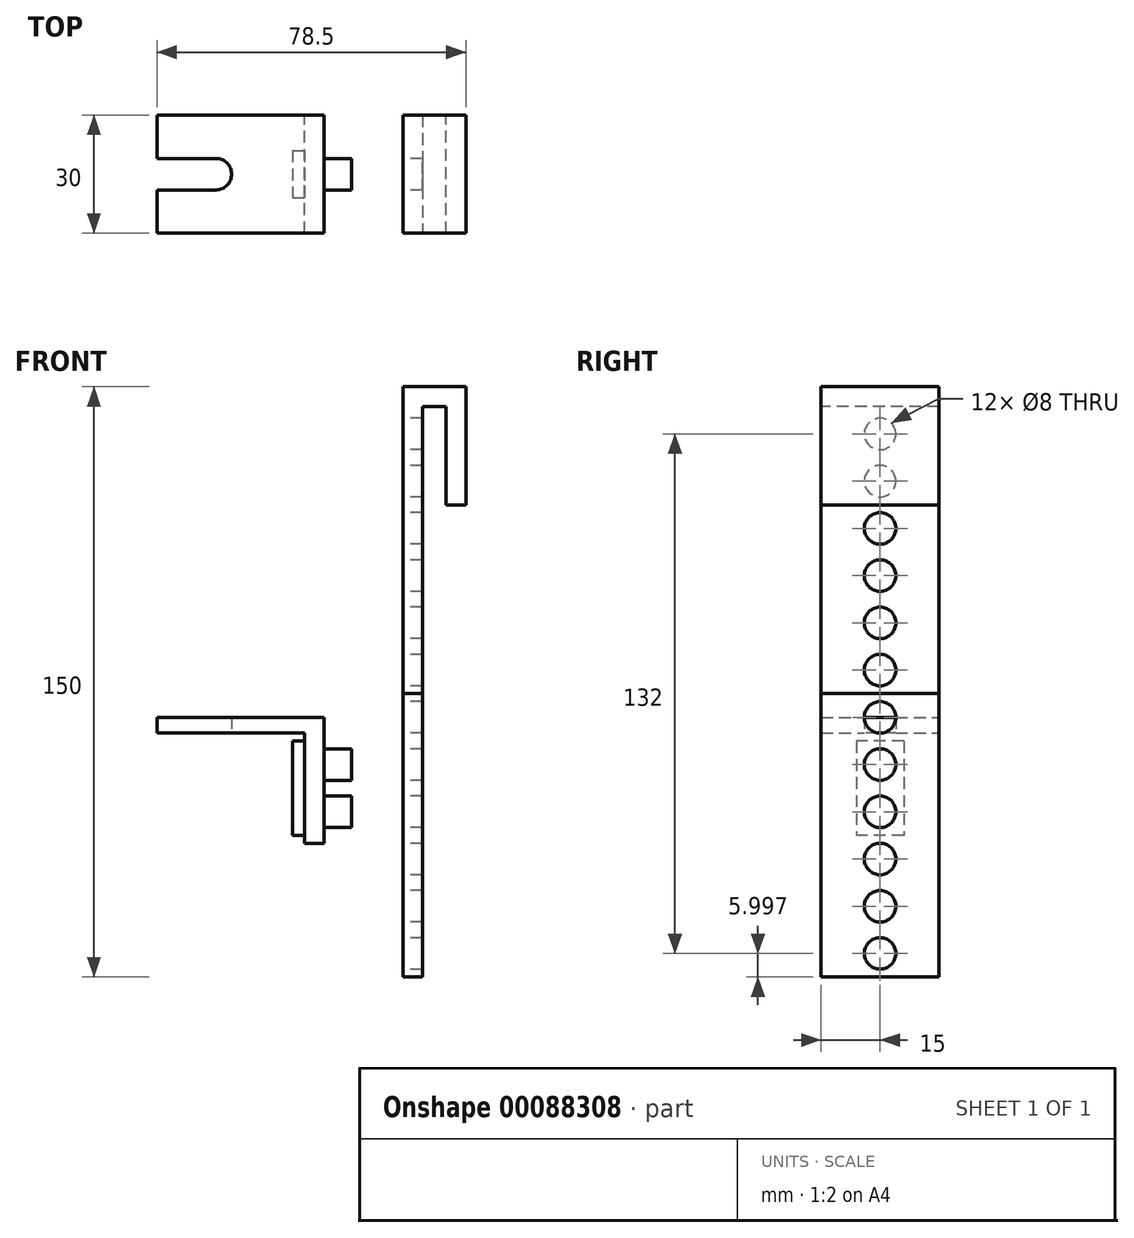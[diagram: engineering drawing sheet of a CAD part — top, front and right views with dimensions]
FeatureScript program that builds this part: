
annotation { "Feature Type Name" : "Feature", "Feature Type Description" : "" }
export const myFeature = defineFeature(function(context is Context, id is Id, definition is map)
    precondition{}
    {
        {
            var Q0;
            Q0=qCreatedBy(makeId("Right.planeOp"),FACE);
            var sketch = newSketch(context, id + "F0", { "sketchPlane" : qUnion([Q0])});
            skLineSegment(sketch, "E0.0", {"start": v(-15, 66.87) * mm, "end": v(15, 66.87) * mm});
            skLineSegment(sketch, "E1.0", {"start": v(-15, -83.13) * mm, "end": v(-15, 66.87) * mm});
            skLineSegment(sketch, "E2", {"start": v(15, -29.13) * mm, "end": v(-15, -29.13) * mm, "construction": true});
            skLineSegment(sketch, "E3", {"start": v(15, 66.87) * mm, "end": v(15, -29.13) * mm, "construction": true});
            skLineSegment(sketch, "E4", {"start": v(15, 18.87) * mm, "end": v(-15, 18.87) * mm, "construction": true});
            skLineSegment(sketch, "E5", {"start": v(15, 18.87) * mm, "end": v(15, -29.13) * mm, "construction": true});
            skLineSegment(sketch, "E6", {"start": v(15, -5.13) * mm, "end": v(-15, -5.13) * mm, "construction": true});
            skLineSegment(sketch, "E7", {"start": v(15, 18.87) * mm, "end": v(15, -5.13) * mm, "construction": true});
            skLineSegment(sketch, "E8", {"start": v(15, 6.87) * mm, "end": v(-15, 6.87) * mm, "construction": true});
            skLineSegment(sketch, "E9.MirrorCS", {"start": v(15, -17.13) * mm, "end": v(-15, -17.13) * mm, "construction": true});
            skLineSegment(sketch, "E10.MirrorCS", {"start": v(15, -41.13) * mm, "end": v(-15, -41.13) * mm, "construction": true});
            skLineSegment(sketch, "E11.MirrorCS", {"start": v(15, -53.13) * mm, "end": v(-15, -53.13) * mm, "construction": true});
            skLineSegment(sketch, "E12.MirrorCS", {"start": v(15, -65.13) * mm, "end": v(-15, -65.13) * mm, "construction": true});
            skLineSegment(sketch, "E13.MirrorCS", {"start": v(15, -77.13) * mm, "end": v(-15, -77.13) * mm, "construction": true});
            skLineSegment(sketch, "E14", {"start": v(0, 66.87) * mm, "end": v(0, -125.13) * mm, "construction": true});
            skCircle(sketch, "E15", {"center": v(0, -41.13) * mm, "radius": 4 * mm});
            skCircle(sketch, "E16.MirrorC", {"center": v(0, -17.13) * mm, "radius": 4 * mm});
            skCircle(sketch, "E17.MirrorC", {"center": v(0, 6.87) * mm, "radius": 4 * mm});
            skCircle(sketch, "E18.MirrorC", {"center": v(0, -65.13) * mm, "radius": 4 * mm});
            skCircle(sketch, "E19", {"center": v(0, -29.13) * mm, "radius": 4 * mm});
            skCircle(sketch, "E20.MirrorC", {"center": v(0, -53.13) * mm, "radius": 4 * mm});
            skCircle(sketch, "E21.MirrorC", {"center": v(0, -77.13) * mm, "radius": 4 * mm});
            skCircle(sketch, "E22.MirrorC", {"center": v(0, -5.13) * mm, "radius": 4 * mm});
            skCircle(sketch, "E23.MirrorC", {"center": v(0, 18.87) * mm, "radius": 4 * mm});
            skLineSegment(sketch, "E24.trimOffspring", {"start": v(15, -89.13) * mm, "end": v(15, 66.87) * mm});
            skCircle(sketch, "E25", {"center": v(0, 30.87) * mm, "radius": 4 * mm});
            skCircle(sketch, "E26", {"center": v(0, 42.87) * mm, "radius": 4 * mm});
            skCircle(sketch, "E27", {"center": v(0, 54.87) * mm, "radius": 4 * mm});
            skLineSegment(sketch, "E28", {"start": v(15, -11.13) * mm, "end": v(-15, -11.13) * mm});
            skLineSegment(sketch, "E29", {"start": v(15, -77.13) * mm, "end": v(15, -83.13) * mm, "construction": true});
            skLineSegment(sketch, "E30", {"start": v(15, -83.13) * mm, "end": v(-15, -83.13) * mm});
            skPoint(sketch, "E31.orphan", {"position": v(-15, -89.13) * mm});
            skSolve(sketch);
        }
        {
            var Q0;
            {var subQ0=sQuery(id+"F0.wireOp",EDGE,"E0.0");Q0=makeQuery(id+"F0.imprint","IMPRINT",FACE,{"disambiguationData":[TD([[makeQuery(id+"F0.imprint","IMPRINT",EDGE,{"derivedFrom":subQ0}),-1.0]])]});}
            extrude(context, id + "F1", {"entities" : qUnion([Q0]), "depth" : 2.5 * mm, "hasSecondDirection" : true, "secondDirectionOppositeDirection" : true, "secondDirectionDepth" : 2.5 * mm});
        }
        {
            var Q0;
            Q0=makeQuery(id+"F0.imprint","IMPRINT",FACE,{"disambiguationData":[TD([[makeQuery(id+"F0.imprint","IMPRINT",EDGE,{"derivedFrom":sQuery(id+"F0.wireOp",EDGE,"E15")}),-1.0]])]});
            extrude(context, id + "F2", {"entities" : qUnion([Q0]), "depth" : 2.5 * mm, "hasSecondDirection" : true, "secondDirectionOppositeDirection" : true, "secondDirectionDepth" : 2.5 * mm});
        }
        {
            var Q0;
            Q0=qCreatedBy(makeId("Front.planeOp"),FACE);
            var sketch = newSketch(context, id + "F3", { "sketchPlane" : qUnion([Q0])});
            skLineSegment(sketch, "E32.0", {"start": v(-2.5, 66.87) * mm, "end": v(2.5, 66.87) * mm});
            skLineSegment(sketch, "E33.0", {"start": v(-2.5, 61.87) * mm, "end": v(-2.5, 66.87) * mm});
            skLineSegment(sketch, "E34.bottom", {"start": v(-2.5, 66.87) * mm, "end": v(13.5, 66.87) * mm});
            skLineSegment(sketch, "E34.top", {"start": v(-2.5, 61.87) * mm, "end": v(8.5, 61.87) * mm});
            skLineSegment(sketch, "E34.left", {"start": v(-2.5, 66.87) * mm, "end": v(-2.5, 61.87) * mm});
            skLineSegment(sketch, "E34.right", {"start": v(13.5, 66.87) * mm, "end": v(13.5, 61.87) * mm});
            skLineSegment(sketch, "E35.bottom", {"start": v(13.5, 66.87) * mm, "end": v(8.5, 66.87) * mm});
            skLineSegment(sketch, "E35.top", {"start": v(13.5, 36.87) * mm, "end": v(8.5, 36.87) * mm});
            skLineSegment(sketch, "E35.left", {"start": v(13.5, 66.87) * mm, "end": v(13.5, 36.87) * mm});
            skLineSegment(sketch, "E35.right", {"start": v(8.5, 61.87) * mm, "end": v(8.5, 36.87) * mm});
            skPoint(sketch, "E36.orphan", {"position": v(-2.5, -55.38) * mm});
            skPoint(sketch, "E37.0.start.orphan", {"position": v(2.5, -75) * mm});
            skLineSegment(sketch, "E38", {"start": v(8.5, 61.87) * mm, "end": v(-2.5, 61.87) * mm});
            skLineSegment(sketch, "E39", {"start": v(2.5, 66.87) * mm, "end": v(8.5, 66.87) * mm});
            skSolve(sketch);
        }
        {
            var Q0;
            Q0=qSketchRegion(id+"F3",true);
            extrude(context, id + "F4", {"entities" : qUnion([Q0]), "operationType" : NewBodyOperationType.ADD, "depth" : 15 * mm, "hasSecondDirection" : true, "secondDirectionOppositeDirection" : true, "secondDirectionDepth" : 15 * mm});
        }
        {
            var Q0;
            Q0=qCreatedBy(makeId("Right.planeOp"),FACE);
            cPlane(context, id + "F5", {"entities" : qUnion([Q0]), "cplaneType" : CPlaneType.OFFSET, "offset" : 25 * mm, "oppositeDirection" : true, "width" : 150 * mm, "height" : 150 * mm});
        }
        {
            var Q0;
            Q0=qCreatedBy(id+"F5.planeOp",FACE);
            var sketch = newSketch(context, id + "F6", { "sketchPlane" : qUnion([Q0])});
            skCircle(sketch, "E40.0", {"center": v(0, -29.13) * mm, "radius": 4 * mm});
            skCircle(sketch, "E41.0", {"center": v(0, -41.13) * mm, "radius": 4 * mm});
            skLineSegment(sketch, "E42.0", {"start": v(-15, 66.87) * mm, "end": v(-15, 66.87) * mm});
            skCircle(sketch, "E43.0", {"center": v(0, -17.13) * mm, "radius": 4 * mm, "construction": true});
            skCircle(sketch, "E44.0", {"center": v(0, -53.13) * mm, "radius": 4 * mm, "construction": true});
            skLineSegment(sketch, "E45", {"start": v(0, -17.13) * mm, "end": v(-15, -17.13) * mm, "construction": true});
            skLineSegment(sketch, "E46", {"start": v(0, -53.13) * mm, "end": v(-15, -53.13) * mm, "construction": true});
            skLineSegment(sketch, "E47", {"start": v(0, -21.13) * mm, "end": v(-15, -21.13) * mm, "construction": true});
            skLineSegment(sketch, "E48", {"start": v(0, -49.13) * mm, "end": v(-15, -49.13) * mm, "construction": true});
            skLineSegment(sketch, "E49.bottom", {"start": v(-15, -49.13) * mm, "end": v(15, -49.13) * mm});
            skLineSegment(sketch, "E49.top", {"start": v(-15, -17.13) * mm, "end": v(15, -17.13) * mm});
            skLineSegment(sketch, "E49.left", {"start": v(-15, -49.13) * mm, "end": v(-15, -17.13) * mm});
            skLineSegment(sketch, "E49.right", {"start": v(15, -49.13) * mm, "end": v(15, -17.13) * mm});
            skLineSegment(sketch, "E50.top", {"start": v(-15, -21.13) * mm, "end": v(15, -21.13) * mm});
            skLineSegment(sketch, "E50.left", {"start": v(-15, -17.13) * mm, "end": v(-15, -21.13) * mm});
            skLineSegment(sketch, "E50.right", {"start": v(15, -17.13) * mm, "end": v(15, -21.13) * mm});
            skSolve(sketch);
        }
        {
            var Q0;
            Q0=qSketchRegion(id+"F6",true);
            extrude(context, id + "F7", {"entities" : qUnion([Q0]), "depth" : 2.5 * mm, "hasSecondDirection" : true, "secondDirectionOppositeDirection" : true, "secondDirectionDepth" : 2.5 * mm});
        }
        {
            var Q0;
            Q0=makeQuery(id+"F6.imprint","IMPRINT",FACE,{"disambiguationData":[TD([[makeQuery(id+"F6.imprint","IMPRINT",EDGE,{"derivedFrom":sQuery(id+"F6.wireOp",EDGE,"E49.top")}),-1.0]])]});
            extrude(context, id + "F8", {"entities" : qUnion([Q0]), "operationType" : NewBodyOperationType.ADD, "oppositeDirection" : true, "depth" : 40 * mm});
        }
        {
            var Q0;
            {var subQ0=sQuery(id+"F6.wireOp",EDGE,"E49.top");Q0=makeQuery(id+"F8.boolean.opBoolean","MERGE",FACE,{"derivedFrom":[makeQuery(id+"F7.opExtrude","SWEPT_FACE",FACE,{"disambiguationData":[OSD([subQ0])]}),makeQuery(id+"F8.opExtrude","SWEPT_FACE",FACE,{"disambiguationData":[OSD([subQ0])]})]});}
            var sketch = newSketch(context, id + "F9", { "sketchPlane" : qUnion([Q0])});
            skLineSegment(sketch, "E51.0", {"start": v(-22.5, 15) * mm, "end": v(-65, 15) * mm, "construction": true});
            skLineSegment(sketch, "E52.0", {"start": v(-65, -15) * mm, "end": v(-65, 15) * mm, "construction": true});
            skLineSegment(sketch, "E53.0", {"start": v(-22.5, -15) * mm, "end": v(-65, -15) * mm, "construction": true});
            skLineSegment(sketch, "E54.bottom", {"start": v(-65, 15) * mm, "end": v(-35, 15) * mm, "construction": true});
            skLineSegment(sketch, "E54.top", {"start": v(-65, -15) * mm, "end": v(-35, -15) * mm, "construction": true});
            skLineSegment(sketch, "E54.left", {"start": v(-65, 15) * mm, "end": v(-65, -15) * mm, "construction": true});
            skLineSegment(sketch, "E54.right", {"start": v(-35, 15) * mm, "end": v(-35, -15) * mm, "construction": true});
            skLineSegment(sketch, "E55", {"start": v(-50, 15) * mm, "end": v(-50, -15) * mm, "construction": true});
            skLineSegment(sketch, "E56", {"start": v(-65, 0) * mm, "end": v(-35, 0) * mm, "construction": true});
            skCircle(sketch, "E57", {"center": v(-50, 0) * mm, "radius": 4 * mm});
            skLineSegment(sketch, "E58", {"start": v(-50, 4) * mm, "end": v(-65, 4) * mm});
            skLineSegment(sketch, "E59", {"start": v(-50, -4) * mm, "end": v(-65, -4) * mm});
            skLineSegment(sketch, "E60", {"start": v(-65, -4) * mm, "end": v(-65, 4) * mm});
            skSolve(sketch);
        }
        {
            var Q0;
            Q0=qSketchRegion(id+"F9",true);
            extrude(context, id + "F10", {"entities" : qUnion([Q0]), "operationType" : NewBodyOperationType.REMOVE, "depth" : 5 * mm, "hasSecondDirection" : true, "secondDirectionOppositeDirection" : true, "secondDirectionDepth" : 5 * mm});
        }
        {
            var Q0;
            Q0=makeQuery(id+"F7.opExtrude","CAP_FACE",FACE,{"disambiguationData":[OSD([sQuery(id+"F6.wireOp",EDGE,"E40.0"),sQuery(id+"F6.wireOp",EDGE,"E41.0"),sQuery(id+"F6.wireOp",EDGE,"E49.bottom"),sQuery(id+"F6.wireOp",EDGE,"E49.left"),sQuery(id+"F6.wireOp",EDGE,"E49.right"),sQuery(id+"F6.wireOp",EDGE,"E49.top"),sQuery(id+"F6.wireOp",EDGE,"E50.left"),sQuery(id+"F6.wireOp",EDGE,"E50.right")])],"isStart":true});
            var sketch = newSketch(context, id + "F11", { "sketchPlane" : qUnion([Q0])});
            skCircle(sketch, "E61", {"center": v(0, -29.13) * mm, "radius": 4 * mm, "construction": true});
            skCircle(sketch, "E62", {"center": v(0, -41.13) * mm, "radius": 4 * mm, "construction": true});
            skLineSegment(sketch, "E63.bottom", {"start": v(-6, -23.13) * mm, "end": v(6, -23.13) * mm});
            skLineSegment(sketch, "E63.top", {"start": v(-6, -47.13) * mm, "end": v(6, -47.13) * mm});
            skLineSegment(sketch, "E63.left", {"start": v(-6, -23.13) * mm, "end": v(-6, -47.13) * mm});
            skLineSegment(sketch, "E63.right", {"start": v(6, -23.13) * mm, "end": v(6, -47.13) * mm});
            skSolve(sketch);
        }
        {
            var Q0;
            Q0=qSketchRegion(id+"F11",true);
            extrude(context, id + "F12", {"entities" : qUnion([Q0]), "depth" : 3 * mm});
        }
        {
            var Q0;
            Q0=makeQuery(id+"F11.imprint","IMPRINT",FACE,{"disambiguationData":[TD([[makeQuery(id+"F11.imprint","IMPRINT",EDGE,{"derivedFrom":makeQuery(id+"F7.opExtrude","CAP_EDGE",EDGE,{"disambiguationData":[OSD([sQuery(id+"F6.wireOp",EDGE,"E40.0")])],"isStart":true})}),-1.0]])]});
            var Q1;
            Q1=makeQuery(id+"F11.imprint","IMPRINT",FACE,{"disambiguationData":[TD([[makeQuery(id+"F11.imprint","IMPRINT",EDGE,{"derivedFrom":makeQuery(id+"F7.opExtrude","CAP_EDGE",EDGE,{"disambiguationData":[OSD([sQuery(id+"F6.wireOp",EDGE,"E41.0")])],"isStart":true})}),-1.0]])]});
            extrude(context, id + "F13", {"entities" : qUnion([Q0, Q1]), "operationType" : NewBodyOperationType.ADD, "oppositeDirection" : true, "depth" : 12 * mm, "hasSecondDirection" : true, "secondDirectionOppositeDirection" : false, "secondDirectionDepth" : 3 * mm});
        }
        {
            var Q0;
            Q0 = qSketchRegion(id + "F9", true);
            extrude(context, id + "F14", {"entities" : qUnion([Q0]), "operationType" : NewBodyOperationType.REMOVE, "oppositeDirection" : true, "depth" : 5 * mm});
        }
    });
